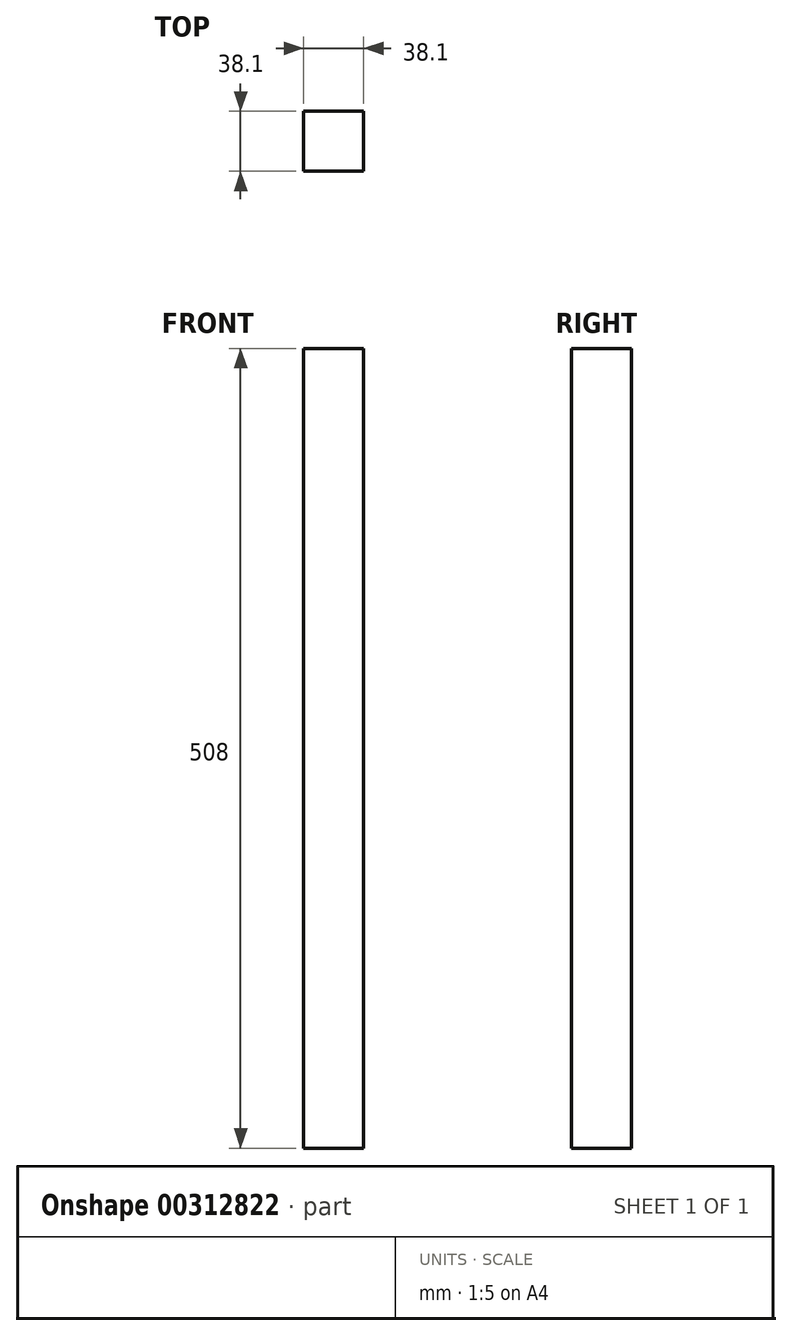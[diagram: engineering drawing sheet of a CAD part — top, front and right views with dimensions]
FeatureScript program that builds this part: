
annotation { "Feature Type Name" : "Feature", "Feature Type Description" : "" }
export const myFeature = defineFeature(function(context is Context, id is Id, definition is map)
    precondition{}
    {
        {
            var Q0;
            Q0=qCreatedBy(makeId("Front.planeOp"),FACE);
            var sketch = newSketch(context, id + "F0", { "sketchPlane" : qUnion([Q0])});
            skLineSegment(sketch, "E0.bottom", {"start": v(-69, 337.93) * mm, "end": v(-107.1, 337.93) * mm});
            skLineSegment(sketch, "E0.top", {"start": v(-69, -170.07) * mm, "end": v(-107.1, -170.07) * mm});
            skLineSegment(sketch, "E0.left", {"start": v(-69, 337.93) * mm, "end": v(-69, -170.07) * mm});
            skLineSegment(sketch, "E0.right", {"start": v(-107.1, 337.93) * mm, "end": v(-107.1, -170.07) * mm});
            skSolve(sketch);
        }
        {
            var Q0;
            Q0 = qSketchRegion(id + "F0", true);
            extrude(context, id + "F1", {"entities" : qUnion([Q0]), "depth" : 38.1 * mm});
        }
    });
